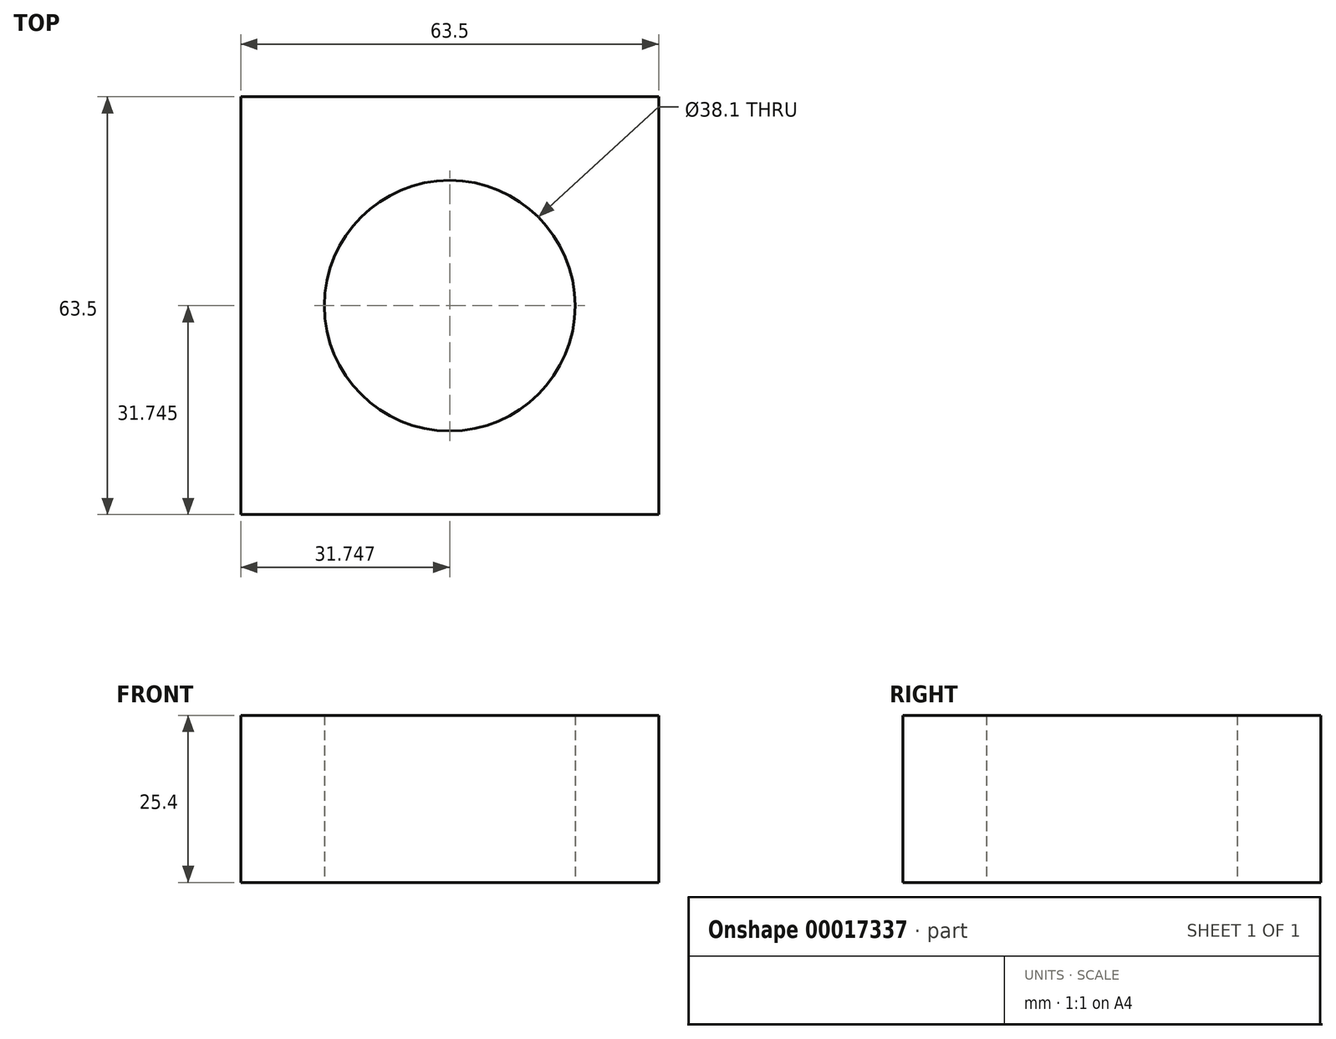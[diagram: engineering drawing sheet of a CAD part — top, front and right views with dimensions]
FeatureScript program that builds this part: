
annotation { "Feature Type Name" : "Feature", "Feature Type Description" : "" }
export const myFeature = defineFeature(function(context is Context, id is Id, definition is map)
    precondition{}
    {
        {
            var Q0;
            Q0=qCreatedBy(makeId("Top.planeOp"),FACE);
            var sketch = newSketch(context, id + "F0", { "sketchPlane" : qUnion([Q0])});
            skLineSegment(sketch, "E0", {"start": v(-39.28, 39.12) * mm, "end": v(-39.28, -24.38) * mm});
            skLineSegment(sketch, "E1", {"start": v(-39.28, -24.38) * mm, "end": v(24.22, -24.38) * mm});
            skLineSegment(sketch, "E2", {"start": v(24.22, -24.38) * mm, "end": v(24.22, 39.12) * mm});
            skLineSegment(sketch, "E3", {"start": v(24.22, 39.12) * mm, "end": v(-39.28, 39.12) * mm});
            skCircle(sketch, "E4", {"center": v(-7.53, 7.37) * mm, "radius": 19.05 * mm});
            skSolve(sketch);
        }
        {
            var Q0;
            Q0 = qSketchRegion(id + "F0", true);
            extrude(context, id + "F1", {"entities" : qUnion([Q0]), "depth" : 25.4 * mm});
        }
    });
